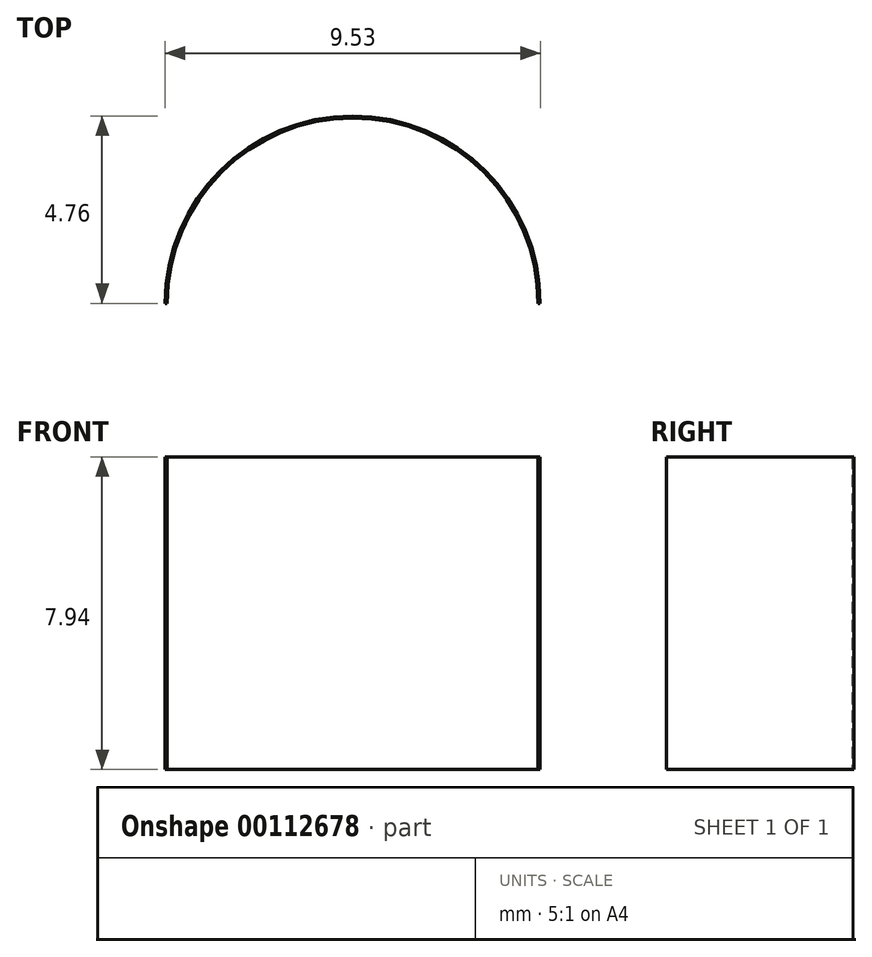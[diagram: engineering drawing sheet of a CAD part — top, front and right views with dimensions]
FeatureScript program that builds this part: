
annotation { "Feature Type Name" : "Feature", "Feature Type Description" : "" }
export const myFeature = defineFeature(function(context is Context, id is Id, definition is map)
    precondition{}
    {
        {
            var Q0;
            Q0=qCreatedBy(makeId("Top.planeOp"),FACE);
            var sketch = newSketch(context, id + "F0", { "sketchPlane" : qUnion([Q0])});
            skLineSegment(sketch, "E0", {"start": v(0, 0) * mm, "end": v(0.05, 0) * mm});
            skLineSegment(sketch, "E1", {"start": v(0.05, 0) * mm, "end": v(9.47, 0) * mm, "construction": true});
            skLineSegment(sketch, "E2", {"start": v(9.47, 0) * mm, "end": v(9.53, 0) * mm});
            skArc(sketch, "E3", {"start": v(9.53, 0) * mm, "mid": v(4.76, 4.76) * mm, "end": v(0, 0) * mm});
            skArc(sketch, "E4", {"start": v(9.47, 0) * mm, "mid": v(4.76, 4.71) * mm, "end": v(0.05, 0) * mm});
            skSolve(sketch);
        }
        {
            var Q0;
            Q0 = qSketchRegion(id + "F0", true);
            extrude(context, id + "F1", {"entities" : qUnion([Q0]), "depth" : 7.94 * mm});
        }
    });
